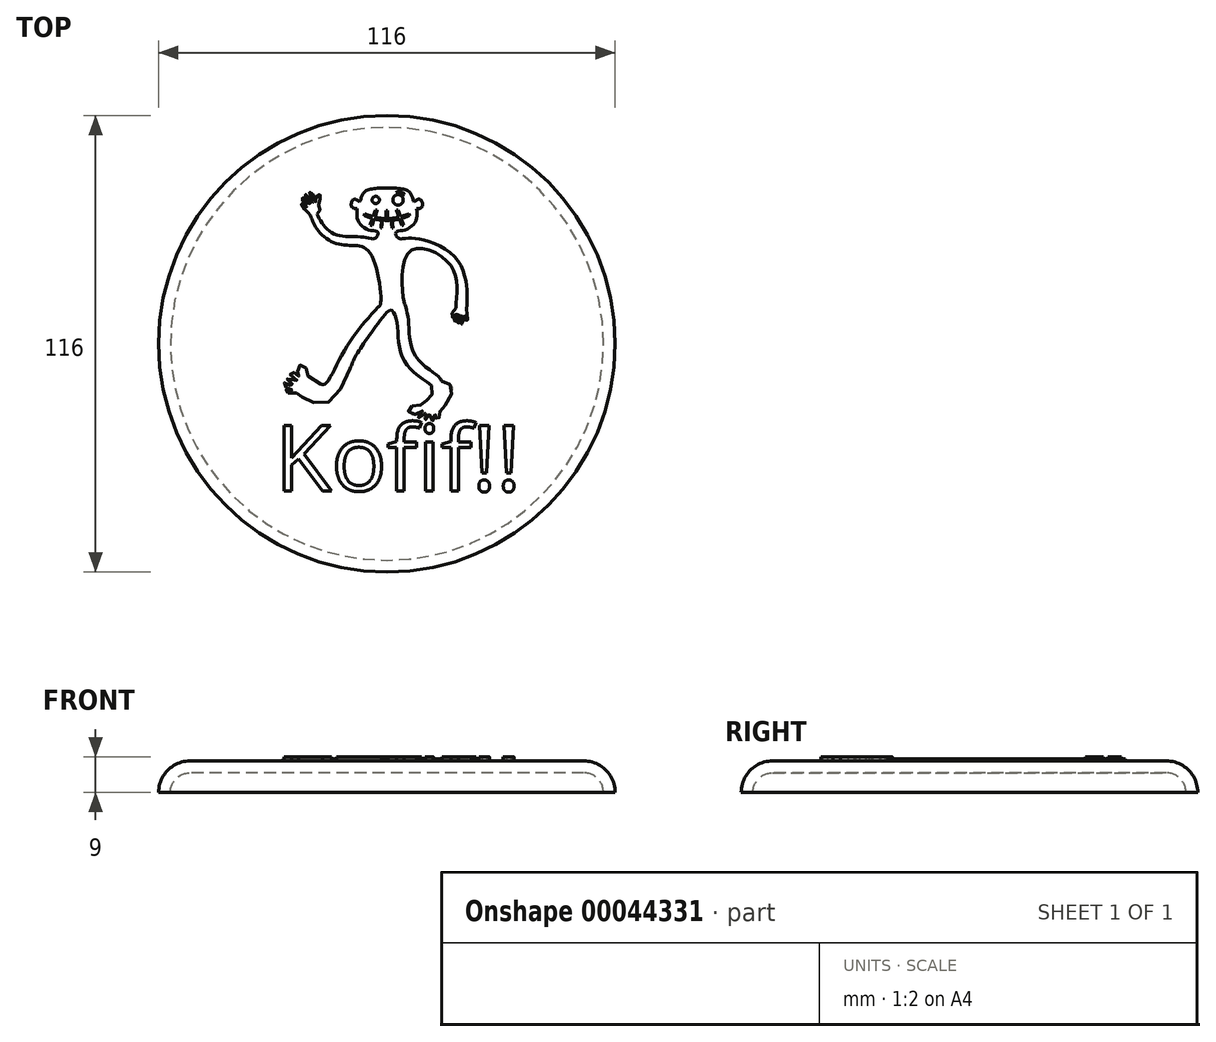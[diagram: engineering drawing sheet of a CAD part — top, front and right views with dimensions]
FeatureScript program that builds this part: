
annotation { "Feature Type Name" : "Feature", "Feature Type Description" : "" }
export const myFeature = defineFeature(function(context is Context, id is Id, definition is map)
    precondition{}
    {
        {
            var Q0;
            Q0=qCreatedBy(makeId("Front.planeOp"),FACE);
            var sketch = newSketch(context, id + "F0", { "sketchPlane" : qUnion([Q0])});
            skLineSegment(sketch, "E0", {"start": v(0, 5) * mm, "end": v(-50, 5) * mm});
            skLineSegment(sketch, "E1", {"start": v(0, 8) * mm, "end": v(-50, 8) * mm});
            skArc(sketch, "E2", {"start": v(-50, 5) * mm, "mid": v(-53.54, 3.54) * mm, "end": v(-55, 0) * mm});
            skArc(sketch, "E3", {"start": v(-50, 8) * mm, "mid": v(-55.66, 5.66) * mm, "end": v(-58, 0) * mm});
            skLineSegment(sketch, "E4", {"start": v(0, 8) * mm, "end": v(0, 5) * mm});
            skLineSegment(sketch, "E5", {"start": v(-58, 0) * mm, "end": v(-55, 0) * mm});
            skSolve(sketch);
        }
        {
            var Q0;
            Q0 = qSketchRegion(id + "F0", true);
            var Q1;
            Q1=sQuery(id+"F0.wireOp",EDGE,"E4");
            revolve(context, id + "F1", {"entities" : qUnion([Q0]), "axis" : qUnion([Q1]), "revolveType" : RevolveType.FULL});
        }
        {
            var Q0;
            Q0=makeQuery(id+"F1.opRevolve","SWEPT_FACE",FACE,{"disambiguationData":[OSD([sQuery(id+"F0.wireOp",EDGE,"E1")])]});
            var sketch = newSketch(context, id + "F2", { "sketchPlane" : qUnion([Q0])});
            skText(sketch, "E6", { "text": "Kofif!!", "fontName": "OpenSans-Regular.ttf"});
            skFitSpline(sketch, "E7", {"points": [v(-16.84, -10.22) * mm, v(-20.66, -7.31) * mm, v(-20.66, -5.74) * mm, v(-22.44, -5.6) * mm, v(-22.69, -7.07) * mm, v(-22.23, -7.9) * mm, v(-22.48, -8.3) * mm, v(-23.5, -7.42) * mm, v(-24.05, -7.17) * mm, v(-24.54, -7.77) * mm, v(-22.86, -9.3) * mm, v(-23.18, -9.59) * mm, v(-24.58, -8.75) * mm, v(-25.03, -8.68) * mm, v(-25.45, -9.27) * mm, v(-23.63, -10.46) * mm, v(-23.91, -10.7) * mm, v(-25.66, -10) * mm, v(-25.98, -9.94) * mm, v(-26.33, -10.81) * mm, v(-24.09, -11.48) * mm, v(-24.09, -11.76) * mm, v(-25.2, -11.62) * mm, v(-25.66, -11.69) * mm, v(-25.56, -12.32) * mm, v(-23.8, -12.42) * mm, v(-22.44, -12.84) * mm, v(-21.25, -13.79) * mm, v(-15.51, -15.12) * mm, v(-9.32, -6.26) * mm], "startDerivative": vector(-84.9, 44.33) * mm, "endDerivative": vector(54.61, 126.57) * mm});
            skFitSpline(sketch, "E8", {"points": [v(-16.84, -10.22) * mm, v(-15.72, -10.22) * mm, v(-10.54, -1.27) * mm, v(-2.24, 9.32) * mm], "startDerivative": vector(7.98, -2.98) * mm, "endDerivative": vector(19, 20.76) * mm});
            skFitSpline(sketch, "E9", {"points": [v(-9.32, -6.26) * mm, v(-7.72, -2.74) * mm, v(-0.54, 7.44) * mm], "startDerivative": vector(3.28, 8.76) * mm, "endDerivative": vector(13.33, 17.79) * mm});
            skFitSpline(sketch, "E10", {"points": [v(-0.54, 7.44) * mm, v(1.02, 8.53) * mm, v(2.5, 5.6) * mm, v(3.96, -3.53) * mm, v(11.4, -10.56) * mm], "startDerivative": vector(11.01, 11.97) * mm, "endDerivative": vector(27, -17.99) * mm});
            skFitSpline(sketch, "E11", {"points": [v(11.4, -10.56) * mm, v(11.4, -13.12) * mm, v(9.7, -14.74) * mm, v(8.25, -15.66) * mm, v(5.94, -16) * mm, v(5.55, -17.31) * mm, v(7.16, -17.94) * mm, v(9.08, -17.08) * mm, v(9.31, -17.31) * mm, v(7.56, -18.34) * mm, v(8.42, -18.83) * mm, v(9.94, -17.58) * mm, v(10.3, -17.84) * mm, v(9.31, -18.93) * mm, v(10.14, -19.23) * mm, v(10.9, -17.94) * mm, v(11.4, -18.07) * mm, v(10.93, -19.4) * mm, v(11.69, -19.56) * mm, v(12.22, -18.07) * mm, v(12.68, -18.1) * mm, v(12.42, -18.97) * mm, v(12.94, -19.2) * mm, v(13.47, -18) * mm, v(13.57, -17.08) * mm, v(15.36, -14.94) * mm, v(16.38, -10.58) * mm, v(13.94, -9.49) * mm], "startDerivative": vector(10.13, -55.49) * mm, "endDerivative": vector(-23, 58.24) * mm});
            skFitSpline(sketch, "E12", {"points": [v(13.94, -9.49) * mm, v(13.05, -8.33) * mm, v(7.04, -2.71) * mm, v(5.46, 5.94) * mm, v(4.6, 9.9) * mm], "startDerivative": vector(-4, 7.7) * mm, "endDerivative": vector(-4.78, 15.59) * mm});
            skFitSpline(sketch, "E13", {"points": [v(-2.24, 9.32) * mm, v(-1.61, 10.17) * mm, v(-4.2, 22.92) * mm, v(-8.09, 24.97) * mm], "startDerivative": vector(4.95, 2.55) * mm, "endDerivative": vector(-13.39, 1.47) * mm});
            skFitSpline(sketch, "E14", {"points": [v(4.6, 9.9) * mm, v(4.4, 10.45) * mm, v(5.63, 23.27) * mm, v(15.72, 20.52) * mm, v(17.68, 11.65) * mm], "startDerivative": vector(-2.42, 3.42) * mm, "endDerivative": vector(-2.4, -32.92) * mm});
            skFitSpline(sketch, "E15", {"points": [v(-8.09, 24.97) * mm, v(-13.67, 25.78) * mm, v(-18, 29.48) * mm, v(-19.4, 32.57) * mm], "startDerivative": vector(-15.96, 0.17) * mm, "endDerivative": vector(-3.65, 10.78) * mm});
            skFitSpline(sketch, "E16", {"points": [v(3.96, 26.66) * mm, v(2.82, 26.93) * mm, v(2.29, 28.34) * mm, v(4.32, 28.87) * mm, v(7.23, 30.98) * mm, v(7.58, 34.33) * mm], "startDerivative": vector(-8.3, -0.3) * mm, "endDerivative": vector(-1.03, 14.46) * mm});
            skFitSpline(sketch, "E17", {"points": [v(7.58, 34.33) * mm, v(9, 34.86) * mm, v(8.5, 36.64) * mm, v(6.92, 36.1) * mm], "startDerivative": vector(5.76, 0.33) * mm, "endDerivative": vector(-5.22, -3.63) * mm});
            skFitSpline(sketch, "E18", {"points": [v(6.92, 36.1) * mm, v(5.75, 38.52) * mm, v(0, 39.6) * mm], "startDerivative": vector(-2.97, 4.3) * mm, "endDerivative": vector(-10.28, 0.09) * mm});
            skFitSpline(sketch, "E19.MirrorCS", {"points": [v(-6.92, 36.1) * mm, v(-5.75, 38.52) * mm, v(0, 39.6) * mm], "startDerivative": vector(2.97, 4.3) * mm, "endDerivative": vector(10.28, 0.09) * mm});
            skFitSpline(sketch, "E20.MirrorCS", {"points": [v(-7.58, 34.33) * mm, v(-9, 34.86) * mm, v(-8.5, 36.64) * mm, v(-6.92, 36.1) * mm], "startDerivative": vector(-5.76, 0.33) * mm, "endDerivative": vector(5.22, -3.63) * mm});
            skFitSpline(sketch, "E21.MirrorCS", {"points": [v(-3.96, 26.66) * mm, v(-2.82, 26.93) * mm, v(-2.29, 28.34) * mm, v(-4.32, 28.87) * mm, v(-7.23, 30.98) * mm, v(-7.58, 34.33) * mm], "startDerivative": vector(8.3, -0.3) * mm, "endDerivative": vector(1.03, 14.46) * mm});
            skFitSpline(sketch, "E22", {"points": [v(-3.96, 26.66) * mm, v(-7.92, 27.26) * mm, v(-12.6, 27.57) * mm, v(-15.97, 29.94) * mm, v(-17.8, 33) * mm], "startDerivative": vector(-15.41, 3.25) * mm, "endDerivative": vector(-6.3, 13.53) * mm});
            skFitSpline(sketch, "E23", {"points": [v(-17.8, 33) * mm, v(-16.98, 34.03) * mm, v(-17.4, 35.88) * mm, v(-16.78, 37.66) * mm, v(-17.8, 37.7) * mm, v(-18.1, 36.02) * mm, v(-19.14, 38.5) * mm, v(-19.66, 38.31) * mm, v(-18.55, 35.88) * mm, v(-20.4, 37.7) * mm, v(-20.5, 37.98) * mm, v(-20.95, 37.53) * mm, v(-19.48, 35.61) * mm, v(-19.64, 35.35) * mm, v(-21.42, 37.13) * mm, v(-21.65, 36.84) * mm, v(-20.34, 34.77) * mm, v(-21.29, 35.43) * mm, v(-21.76, 35.56) * mm, v(-20.9, 34.3) * mm, v(-19.92, 33.3) * mm, v(-19.4, 32.57) * mm], "startDerivative": vector(20.33, 17.34) * mm, "endDerivative": vector(15.04, -15.04) * mm});
            skFitSpline(sketch, "E24", {"points": [v(17.68, 11.65) * mm, v(17.62, 10.17) * mm, v(17.4, 8.9) * mm, v(16.32, 7.15) * mm, v(16.84, 6.73) * mm, v(17.68, 7.71) * mm, v(17.97, 7.7) * mm, v(17.1, 5.77) * mm, v(17.68, 5.53) * mm, v(18.4, 7.54) * mm, v(18.6, 7.42) * mm, v(18.01, 5.3) * mm, v(18.43, 5) * mm, v(19.06, 7.18) * mm, v(19.27, 7.21) * mm, v(18.92, 5.17) * mm, v(19.27, 5.01) * mm, v(19.74, 7.1) * mm, v(20.01, 7.03) * mm, v(20.05, 5.77) * mm, v(20.45, 5.85) * mm, v(20.33, 7.73) * mm, v(20.17, 8.64) * mm, v(20.37, 10.25) * mm, v(20.37, 11.15) * mm], "startDerivative": vector(-2.55, -46.58) * mm, "endDerivative": vector(-1.4, 21.4) * mm});
            skFitSpline(sketch, "E25", {"points": [v(20.37, 11.15) * mm, v(20.37, 13.12) * mm, v(17.77, 21.48) * mm, v(7.94, 26.66) * mm, v(3.96, 26.66) * mm], "startDerivative": vector(0.46, 10.83) * mm, "endDerivative": vector(-16.4, -2.1) * mm});
            const initialGuessF2  = {"E6": [-0.0284, -0.03737, 1, 0, 0.01676]};
            skSetInitialGuess(sketch, initialGuessF2);
            skSolve(sketch);
        }
        {
            var Q0;
            Q0 = qSketchRegion(id + "F2", true);
            extrude(context, id + "F3", {"entities" : qUnion([Q0]), "operationType" : NewBodyOperationType.ADD, "depth" : 1 * mm});
        }
        {
            var Q0;
            Q0=makeQuery(id+"F3.opExtrude","CAP_FACE",FACE,{"disambiguationData":[OSD([sQuery(id+"F2.wireOp",EDGE,"E7"),sQuery(id+"F2.wireOp",EDGE,"E8"),sQuery(id+"F2.wireOp",EDGE,"E9"),sQuery(id+"F2.wireOp",EDGE,"E10"),sQuery(id+"F2.wireOp",EDGE,"E11"),sQuery(id+"F2.wireOp",EDGE,"E12"),sQuery(id+"F2.wireOp",EDGE,"E13"),sQuery(id+"F2.wireOp",EDGE,"E14"),sQuery(id+"F2.wireOp",EDGE,"E15"),sQuery(id+"F2.wireOp",EDGE,"E16"),sQuery(id+"F2.wireOp",EDGE,"E17"),sQuery(id+"F2.wireOp",EDGE,"E18"),sQuery(id+"F2.wireOp",EDGE,"E19.MirrorCS"),sQuery(id+"F2.wireOp",EDGE,"E20.MirrorCS"),sQuery(id+"F2.wireOp",EDGE,"E21.MirrorCS"),sQuery(id+"F2.wireOp",EDGE,"E22"),sQuery(id+"F2.wireOp",EDGE,"E23"),sQuery(id+"F2.wireOp",EDGE,"E24"),sQuery(id+"F2.wireOp",EDGE,"E25")])],"isStart":false});
            var sketch = newSketch(context, id + "F4", { "sketchPlane" : qUnion([Q0])});
            skFitSpline(sketch, "E26", {"points": [v(-2.34, 33.85) * mm, v(-4.92, 33.91) * mm, v(-5.69, 31.3) * mm, v(-1.17, 29.4) * mm, v(0, 29.3) * mm], "startDerivative": vector(-14.01, 4.33) * mm, "endDerivative": vector(5.07, -0.2) * mm});
            skFitSpline(sketch, "E27", {"points": [v(-2.34, 33.85) * mm, v(-1.65, 33.7) * mm, v(0, 33.79) * mm], "startDerivative": vector(0.93, -0.65) * mm, "endDerivative": vector(3.5, -0.16) * mm});
            skLineSegment(sketch, "E28", {"start": v(-2.9, 34.02) * mm, "end": v(-3.46, 32.35) * mm});
            skLineSegment(sketch, "E29", {"start": v(-2.48, 33.9) * mm, "end": v(-3.06, 32.17) * mm});
            skLineSegment(sketch, "E30", {"start": v(-3.23, 31.72) * mm, "end": v(-3.8, 30.03) * mm});
            skLineSegment(sketch, "E31", {"start": v(-3.64, 31.94) * mm, "end": v(-4.26, 30.2) * mm});
            skLineSegment(sketch, "E32", {"start": v(-1.31, 31.49) * mm, "end": v(-1.55, 29.46) * mm});
            skLineSegment(sketch, "E33", {"start": v(-1.09, 31.47) * mm, "end": v(-1.3, 29.42) * mm});
            skLineSegment(sketch, "E34", {"start": v(-0.19, 33.8) * mm, "end": v(-0.19, 31.8) * mm});
            skPoint(sketch, "E35.0.internal.snap0", {"position": v(-2.77, 33.03) * mm});
            skFitSpline(sketch, "E35", {"points": [v(-5.62, 33.03) * mm, v(-4.36, 32.57) * mm, v(-3.46, 32.35) * mm], "startDerivative": vector(2.4, -0.95) * mm, "endDerivative": vector(1.91, -0.4) * mm});
            skFitSpline(sketch, "E36", {"points": [v(-3.06, 32.17) * mm, v(-1.63, 31.9) * mm, v(-0.19, 31.8) * mm], "startDerivative": vector(2.85, -0.63) * mm, "endDerivative": vector(2.9, -0.1) * mm});
            skFitSpline(sketch, "E37", {"points": [v(-5.8, 32.6) * mm, v(-4.63, 32.13) * mm, v(-3.64, 31.94) * mm], "startDerivative": vector(2.23, -1.02) * mm, "endDerivative": vector(2.07, -0.3) * mm});
            skFitSpline(sketch, "E38", {"points": [v(-3.23, 31.72) * mm, v(-2.26, 31.5) * mm, v(-1.31, 31.49) * mm], "startDerivative": vector(1.92, -0.52) * mm, "endDerivative": vector(1.92, 0.06) * mm});
            skFitSpline(sketch, "E39", {"points": [v(-1.09, 31.47) * mm, v(-0.47, 31.35) * mm, v(0, 31.37) * mm], "startDerivative": vector(1.2, -0.28) * mm, "endDerivative": vector(0.98, 0.09) * mm});
            skFitSpline(sketch, "E40.MirrorCS", {"points": [v(1.09, 31.47) * mm, v(0.47, 31.35) * mm, v(0, 31.37) * mm], "startDerivative": vector(-1.2, -0.28) * mm, "endDerivative": vector(-0.98, 0.09) * mm});
            skFitSpline(sketch, "E41.MirrorCS", {"points": [v(5.8, 32.6) * mm, v(4.63, 32.13) * mm, v(3.64, 31.94) * mm], "startDerivative": vector(-2.23, -1.02) * mm, "endDerivative": vector(-2.07, -0.3) * mm});
            skFitSpline(sketch, "E42.MirrorCS", {"points": [v(3.23, 31.72) * mm, v(2.26, 31.5) * mm, v(1.31, 31.49) * mm], "startDerivative": vector(-1.92, -0.52) * mm, "endDerivative": vector(-1.92, 0.06) * mm});
            skFitSpline(sketch, "E43.MirrorCS", {"points": [v(3.06, 32.17) * mm, v(1.63, 31.9) * mm, v(0.19, 31.8) * mm], "startDerivative": vector(-2.85, -0.63) * mm, "endDerivative": vector(-2.9, -0.1) * mm});
            skFitSpline(sketch, "E44.MirrorCS", {"points": [v(5.62, 33.03) * mm, v(4.36, 32.57) * mm, v(3.46, 32.35) * mm], "startDerivative": vector(-2.4, -0.95) * mm, "endDerivative": vector(-1.91, -0.4) * mm});
            skLineSegment(sketch, "E45.MirrorCS", {"start": v(0.19, 33.8) * mm, "end": v(0.19, 31.8) * mm});
            skPoint(sketch, "E46.MirrorP", {"position": v(2.77, 33.03) * mm});
            skLineSegment(sketch, "E47.MirrorCS", {"start": v(1.09, 31.47) * mm, "end": v(1.3, 29.42) * mm});
            skLineSegment(sketch, "E48.MirrorCS", {"start": v(1.31, 31.49) * mm, "end": v(1.55, 29.46) * mm});
            skLineSegment(sketch, "E49.MirrorCS", {"start": v(3.64, 31.94) * mm, "end": v(4.26, 30.2) * mm});
            skLineSegment(sketch, "E50.MirrorCS", {"start": v(2.9, 34.02) * mm, "end": v(3.46, 32.35) * mm});
            skLineSegment(sketch, "E51.MirrorCS", {"start": v(2.48, 33.9) * mm, "end": v(3.06, 32.17) * mm});
            skLineSegment(sketch, "E52.MirrorCS", {"start": v(3.23, 31.72) * mm, "end": v(3.8, 30.03) * mm});
            skFitSpline(sketch, "E53.MirrorCS", {"points": [v(2.34, 33.85) * mm, v(1.65, 33.7) * mm, v(0, 33.79) * mm], "startDerivative": vector(-0.93, -0.65) * mm, "endDerivative": vector(-3.5, -0.16) * mm});
            skFitSpline(sketch, "E54.MirrorCS", {"points": [v(2.34, 33.85) * mm, v(4.92, 33.91) * mm, v(5.69, 31.3) * mm, v(1.17, 29.4) * mm, v(0, 29.3) * mm], "startDerivative": vector(14.01, 4.33) * mm, "endDerivative": vector(-5.07, -0.2) * mm});
            skCircle(sketch, "E55", {"center": v(-2.84, 36.54) * mm, "radius": 1.33 * mm});
            skCircle(sketch, "E56", {"center": v(-2.84, 36.54) * mm, "radius": 0.92 * mm});
            skArc(sketch, "E57", {"start": v(-2.34, 38.45) * mm, "mid": v(-3.53, 38.59) * mm, "end": v(-4.5, 37.87) * mm});
            skArc(sketch, "E58", {"start": v(-2.34, 38.45) * mm, "mid": v(-3.47, 38.34) * mm, "end": v(-4.5, 37.87) * mm});
            skArc(sketch, "E59.MirrorCS", {"start": v(2.34, 38.45) * mm, "mid": v(3.47, 38.34) * mm, "end": v(4.5, 37.87) * mm});
            skArc(sketch, "E60.MirrorCS", {"start": v(2.34, 38.45) * mm, "mid": v(3.53, 38.59) * mm, "end": v(4.5, 37.87) * mm});
            skCircle(sketch, "E61.MirrorC", {"center": v(2.84, 36.54) * mm, "radius": 1.33 * mm});
            skCircle(sketch, "E62.MirrorC", {"center": v(2.84, 36.54) * mm, "radius": 0.92 * mm});
            skSolve(sketch);
        }
        {
            var Q0;
            {var subQ1=sQuery(id+"F4.wireOp",EDGE,"E29");Q0=makeQuery(id+"F4.imprint","IMPRINT",FACE,{"disambiguationData":[TD([[makeQuery(id+"F4.imprint","IMPRINT",EDGE,{"derivedFrom":subQ1}),1.0]])]});}
            var Q1;
            {var subQ1=sQuery(id+"F4.wireOp",EDGE,"E28");Q1=makeQuery(id+"F4.imprint","IMPRINT",FACE,{"disambiguationData":[TD([[makeQuery(id+"F4.imprint","IMPRINT",EDGE,{"derivedFrom":subQ1}),-1.0]])]});}
            var Q2;
            {var subQ1=sQuery(id+"F4.wireOp",EDGE,"E31");Q2=makeQuery(id+"F4.imprint","IMPRINT",FACE,{"disambiguationData":[TD([[makeQuery(id+"F4.imprint","IMPRINT",EDGE,{"derivedFrom":subQ1}),-1.0]])]});}
            var Q3;
            {var subQ1=sQuery(id+"F4.wireOp",EDGE,"E30");Q3=makeQuery(id+"F4.imprint","IMPRINT",FACE,{"disambiguationData":[TD([[makeQuery(id+"F4.imprint","IMPRINT",EDGE,{"derivedFrom":subQ1}),1.0]])]});}
            var Q4;
            {var subQ4=sQuery(id+"F4.wireOp",EDGE,"E33");Q4=makeQuery(id+"F4.imprint","IMPRINT",FACE,{"disambiguationData":[TD([[makeQuery(id+"F4.imprint","IMPRINT",EDGE,{"derivedFrom":subQ4}),1.0]])]});}
            var Q5;
            {var subQ2=sQuery(id+"F4.wireOp",EDGE,"E41.MirrorCS");Q5=makeQuery(id+"F4.imprint","IMPRINT",FACE,{"disambiguationData":[TD([[makeQuery(id+"F4.imprint","IMPRINT",EDGE,{"derivedFrom":subQ2}),1.0]])]});}
            var Q6;
            Q6=makeQuery(id+"F4.imprint","IMPRINT",FACE,{"disambiguationData":[TD([[makeQuery(id+"F4.imprint","IMPRINT",EDGE,{"derivedFrom":sQuery(id+"F4.wireOp",EDGE,"E42.MirrorCS")}),1.0]])]});
            var Q7;
            Q7=makeQuery(id+"F4.imprint","IMPRINT",FACE,{"disambiguationData":[TD([[makeQuery(id+"F4.imprint","IMPRINT",EDGE,{"derivedFrom":sQuery(id+"F4.wireOp",EDGE,"E43.MirrorCS")}),-1.0]])]});
            var Q8;
            {var subQ2=sQuery(id+"F4.wireOp",EDGE,"E44.MirrorCS");Q8=makeQuery(id+"F4.imprint","IMPRINT",FACE,{"disambiguationData":[TD([[makeQuery(id+"F4.imprint","IMPRINT",EDGE,{"derivedFrom":subQ2}),-1.0]])]});}
            var Q9;
            Q9=makeQuery(id+"F4.imprint","IMPRINT",FACE,{"disambiguationData":[TD([[makeQuery(id+"F4.imprint","IMPRINT",EDGE,{"derivedFrom":sQuery(id+"F4.wireOp",EDGE,"E57")}),1.0]])]});
            var Q10;
            Q10=makeQuery(id+"F4.imprint","IMPRINT",FACE,{"disambiguationData":[TD([[makeQuery(id+"F4.imprint","IMPRINT",EDGE,{"derivedFrom":sQuery(id+"F4.wireOp",EDGE,"E59.MirrorCS")}),1.0]])]});
            var Q11;
            Q11=makeQuery(id+"F4.imprint","IMPRINT",FACE,{"disambiguationData":[TD([[makeQuery(id+"F4.imprint","IMPRINT",EDGE,{"derivedFrom":sQuery(id+"F4.wireOp",EDGE,"E61.MirrorC")}),-1.0]])]});
            var Q12;
            Q12=makeQuery(id+"F4.imprint","IMPRINT",FACE,{"disambiguationData":[TD([[makeQuery(id+"F4.imprint","IMPRINT",EDGE,{"derivedFrom":sQuery(id+"F4.wireOp",EDGE,"E55")}),1.0]])]});
            extrude(context, id + "F5", {"entities" : qUnion([Q0, Q1, Q2, Q3, Q4, Q5, Q6, Q7, Q8, Q9, Q10, Q11, Q12]), "operationType" : NewBodyOperationType.REMOVE, "oppositeDirection" : true, "depth" : 0.5 * mm});
        }
    });
